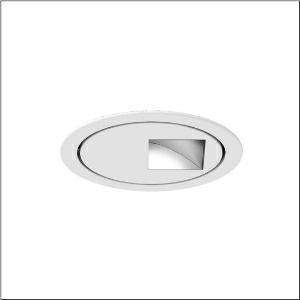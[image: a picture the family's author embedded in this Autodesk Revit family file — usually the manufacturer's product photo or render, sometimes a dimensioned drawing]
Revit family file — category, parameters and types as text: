
# Revit family: lunis_11_mini_round_51dk11b72wg21
name_source: partatom
category: Lighting Fixtures
units: mm (PartAtom-declared; Revit-internal decimal feet)

## family parameters
Cut with Voids When Loaded = No
Host = Face
Light Source = No
Part Type = Normal
Room Calculation Point = No
Round Connector Dimension = Use Diameter
Shared = No

## types (1)
- Lunis 11 mini round (1 x LED 4000K / CRI = 80 (unbekannt), 2470 lm, 4000K)
    Apparent Load = 28 VA
    CIE Flux Codes = 44 77 97 100 100
    Color Rendering = 80
    Color Temperature = 4000K
    Default Elevation = 1800 mm
    Description = Lunis 11 mini round, downlight, light control with wallwasher, of highly reflective aluminium, highly specular, light emission: direct distribution, LED rated luminous flux: 2.470lm, light colour: 840, control gear: ECG, with terminal, 3-pole, mains connection: 220..230V, AC/DC, 0/50..60Hz, LED module, luminaire module, of aluminium, highly specular, white, diameter: 176mm, clamping range: 1..40mm, recessing ring, of plastic, traffic white (RAL 9016), protection rating (complete): IP20, insulation class (complete): insulation class II (safety insulation), certification: CE, permissible ambient temperature for indoor applications: 0..+35°C, packaging unit: 1 piece
    Height = 0 mm  [stored 0 ft]
    Lamp = 1 x LED 4000K / CRI >= 80 (unbekannt)
    Lamp Light Flux = 2470 lm
    Lamp count = 1
    Length = 176 mm
    Luminous efficacy = 88 lm/W
    Manufacturer = Siteco
    ModVariant = No
    Model = 51DK11B72WG21
    Mounting Place = Ceiling
    Mounting Type = Recessed
    Number of Poles = 1
    OnlyDefault = Yes
    Power Factor = 1
    Product Name = Lunis 11 mini round
    Product group = downlight
    ProductGroupID = 400
    Protection Class = Protection class II
    Protection Degree = IP 20
    RLX_Detail_Level = 1
    RLX_Emergency_Light_Flux = 0 lm
    RLX_Emergency_Type = 0
    RLX_Emergency_Type_DB = No
    RlxData = <blob elided: 59345 chars, md5=bb53a126>
    Socket = socket
    Standby Power = 0 W
    System Light Flux = 2470 lm
    System Power = 28 W
    Type Comments = Product without accessories
    Type Image = l_1004772.jpg
    URL = http://relux.com
    VarID = ---
    Voltage = 0 V
    Weight = 0.00 kg
    Width = 176 mm

note: [stored X ft] marks values corroborated as IEEE doubles in the binary element streams (Revit-internal decimal feet)

## geometry (parser evidence)
native form markers: Blend x4, Sweep x12
no freeform markers — native parametric forms only
